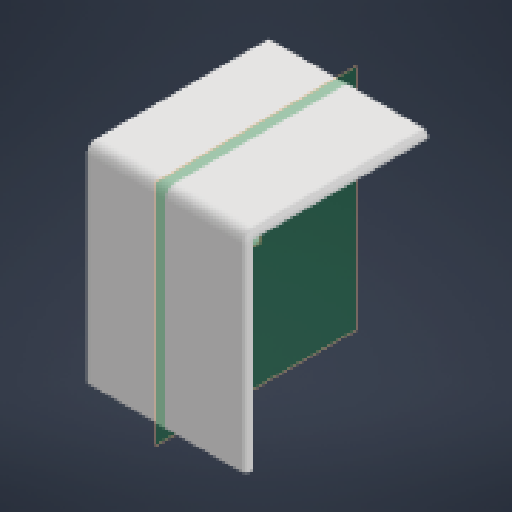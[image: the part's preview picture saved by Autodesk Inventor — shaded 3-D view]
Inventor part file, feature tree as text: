
AUTODESK INVENTOR PART (.ipt)
format: ipt  version: 2024 (Build 280153000, 153)  size: 171,008 bytes
history: native  units: mm
features: reference x13, other x6, extrude x3, sketch x3, mirror x1, fillet x1
ambient origin geometry x8: Origin, YZ Plane, XZ Plane, XY Plane, X Axis, Y Axis, Z Axis, Center Point
bodies: Body1 (feature_tree)
feature tree (27):
  other  "Твердое тело1"
  extrude  "Выдавливание1"  Depth=3.0mm TaperAngle=0.0deg
  other  "РабПлоскость1"
  extrude  "Выдавливание3"  Depth=5.0mm TaperAngle=0.0deg
  extrude  "Выдавливание4"  Depth=3.0mm TaperAngle=0.0deg
  other  "РабПлоскость3"
  mirror  "Зеркальное отражение2"
  fillet  "Сопряжение3"  Radius=4.0mm
  sketch  "Эскиз1"
  reference  "Ссылка2"
  sketch  "Эскиз3"
  reference  "Ссылка7"
  reference  "Ссылка12"
  reference  "Ссылка13"
  reference  "Ссылка14"
  reference  "Ссылка15"
  reference  "Ссылка16"
  reference  "Ссылка17"
  sketch  "Эскиз4"
  reference  "Ссылка18"
  reference  "Ссылка19"
  reference  "Ссылка20"
  reference  "Ссылка21"
  reference  "Ссылка22"
  parser-record x1  (decoder bookkeeping rows leaked as tree rows — omitted from the tree; the rows remain in map.json)
  other  "tail_box_asembly.iam"
  other  "tail_box:1"
note: 1 file-system path scrubbed to <path> (originals preserved in map.json)
